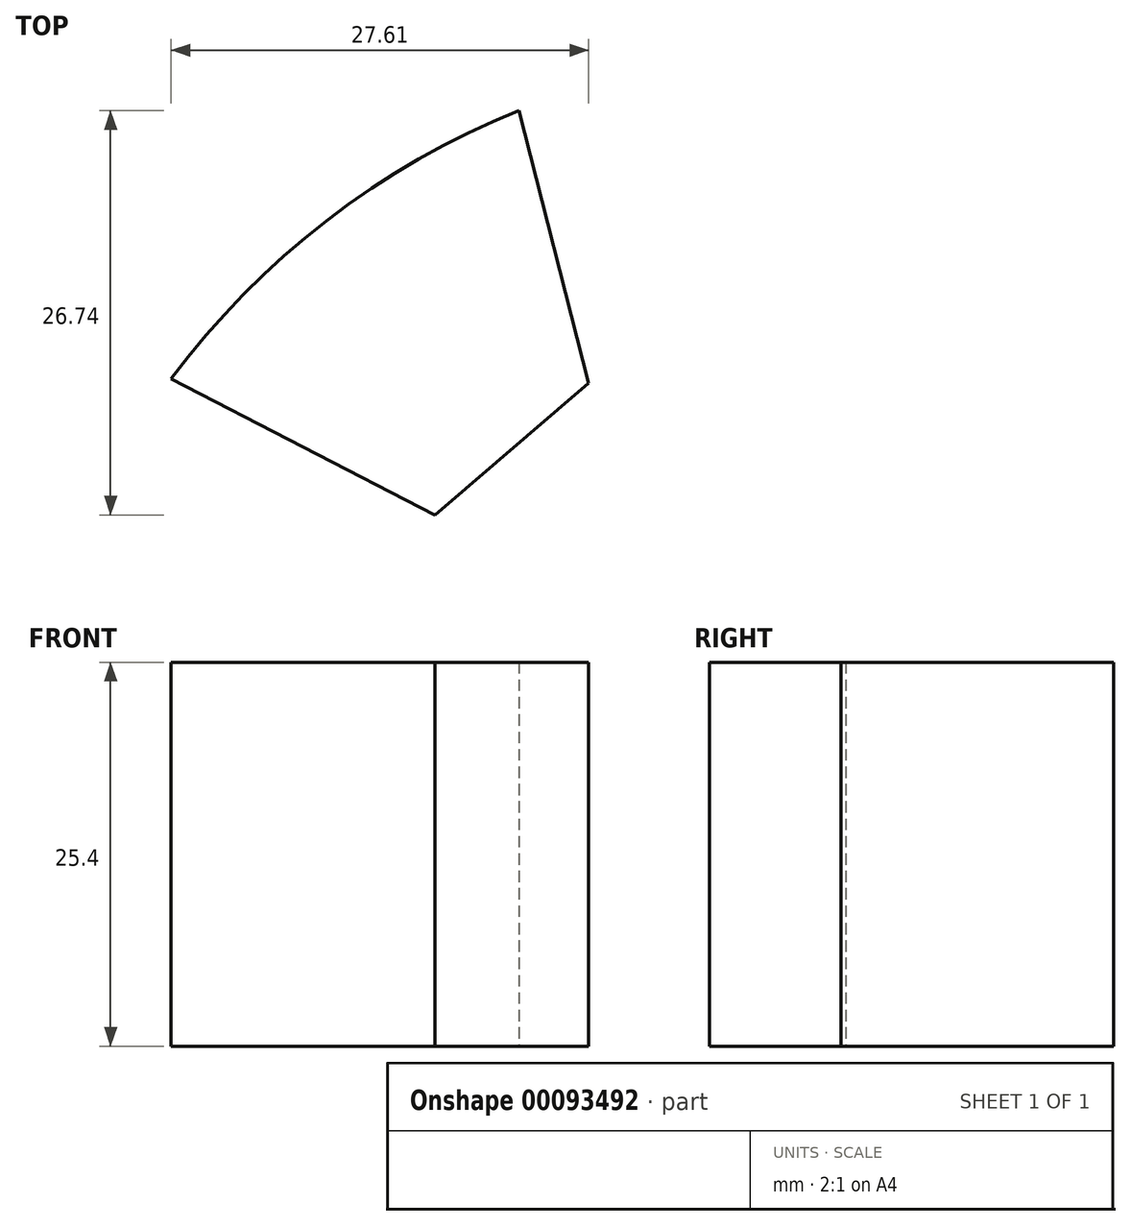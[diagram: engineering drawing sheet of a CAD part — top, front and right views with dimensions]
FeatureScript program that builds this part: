
annotation { "Feature Type Name" : "Feature", "Feature Type Description" : "" }
export const myFeature = defineFeature(function(context is Context, id is Id, definition is map)
    precondition{}
    {
        {
            var Q0;
            Q0=qCreatedBy(makeId("Top.planeOp"),FACE);
            var sketch = newSketch(context, id + "F0", { "sketchPlane" : qUnion([Q0])});
            skCircle(sketch, "E0", {"center": v(0, 0) * mm, "radius": 53.73 * mm});
            skLineSegment(sketch, "E1", {"start": v(-43.09, 32.1) * mm, "end": v(-25.65, 23.09) * mm});
            skLineSegment(sketch, "E2", {"start": v(-25.65, 23.09) * mm, "end": v(-15.48, 31.8) * mm});
            skLineSegment(sketch, "E3", {"start": v(-15.48, 31.8) * mm, "end": v(-20.09, 49.83) * mm});
            skSolve(sketch);
        }
        {
            var Q0;
            {var subQ0=sQuery(id+"F0.wireOp",EDGE,"E1");Q0=makeQuery(id+"F0.imprint","IMPRINT",FACE,{"disambiguationData":[TD([[makeQuery(id+"F0.imprint","IMPRINT",EDGE,{"derivedFrom":subQ0}),1.0]])]});}
            extrude(context, id + "F1", {"entities" : qUnion([Q0]), "depth" : 25.4 * mm});
        }
    });
